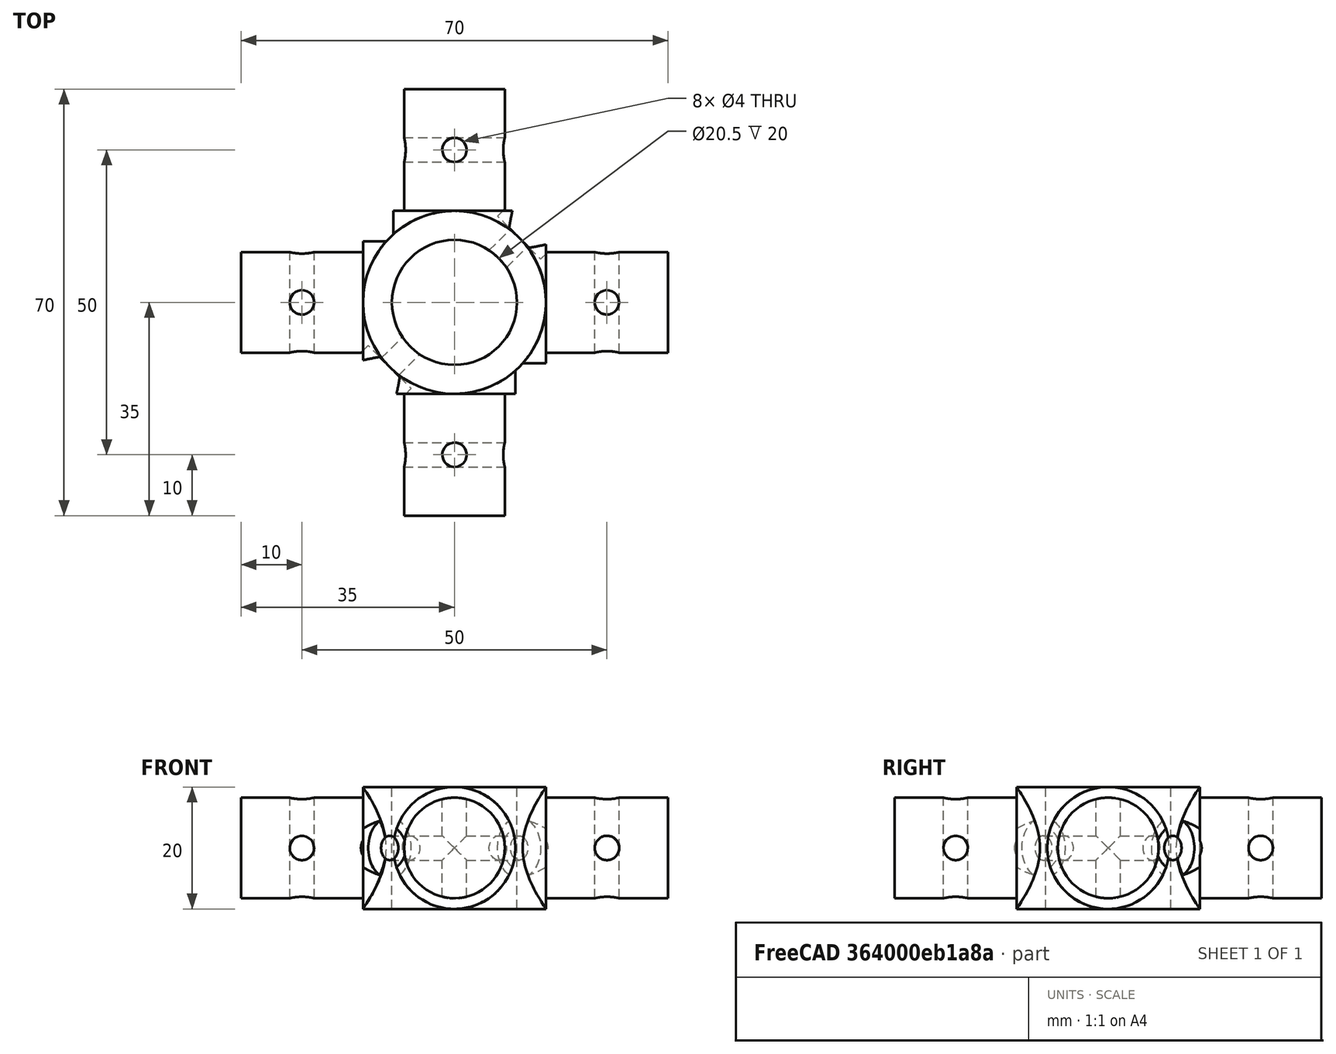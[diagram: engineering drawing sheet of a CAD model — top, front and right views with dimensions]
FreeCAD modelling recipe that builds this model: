
FCSTD DOCUMENT  (FreeCAD 0.18R16110 (Git))
Label: StandCross
License: All rights reserved
LicenseURL: http://en.wikipedia.org/wiki/All_rights_reserved
objects: Part::Cylinder×19, Part::MultiFuse×3, Part::Cut×1
note: 23 computed .brp shape members not serialized (recipe doc carries the construction recipe); baked Part::Feature solids carry a one-line shape summary decoded from their .brp

FEATURE [Part::Cylinder] Cylinder
  Angle = 360
  AttacherType = Attacher::AttachEngine3D
  Height = 20
  Radius = 15
FEATURE [Part::Cylinder] Cylinder001
  Angle = 360
  AttacherType = Attacher::AttachEngine3D
  Height = 20
  Placement = pos=(-15,-8.3e-15,10) rot=(-0.57735,-0.57735,0.57735;2.0944rad)
  Radius = 8.25
FEATURE [Part::Cylinder] Cylinder002
  Angle = 360
  AttacherType = Attacher::AttachEngine3D
  Height = 20
  Placement = pos=(0,15,10) rot=(-1,0,0;1.5708rad)
  Radius = 8.25
FEATURE [Part::Cylinder] Cylinder003
  Angle = 360
  AttacherType = Attacher::AttachEngine3D
  Height = 20
  Placement = pos=(15,5e-15,10) rot=(0.57735,-0.57735,0.57735;4.18879rad)
  Radius = 8.25
FEATURE [Part::Cylinder] Cylinder004
  Angle = 360
  AttacherType = Attacher::AttachEngine3D
  Height = 20
  Placement = pos=(9e-15,-15,10) rot=(0,0.707107,-0.707107;3.14159rad)
  Radius = 8.25
FEATURE [Part::Cylinder] Cylinder005
  Angle = 360
  AttacherType = Attacher::AttachEngine3D
  Height = 30
  Placement = pos=(-15,-3.1e-15,10) rot=(0.57735,-0.57735,0.57735;4.18879rad)
  Radius = 10
FEATURE [Part::Cylinder] Cylinder006
  Angle = 360
  AttacherType = Attacher::AttachEngine3D
  Height = 30
  Placement = pos=(9e-15,-15,10) rot=(-1,0,0;1.5708rad)
  Radius = 10
FEATURE [Part::MultiFuse] Fusion  label="Positive Fusion"
  Shapes = -> [Cylinder,Cylinder005,Cylinder002,Cylinder001,Cylinder003,Cylinder004,Cylinder006]
FEATURE [Part::Cylinder] Cylinder007
  Angle = 360
  AttacherType = Attacher::AttachEngine3D
  Height = 20
  Radius = 10.25
FEATURE [Part::Cylinder] Cylinder009
  Angle = 360
  AttacherType = Attacher::AttachEngine3D
  Height = 30
  Placement = pos=(-15,0,10) rot=(0,1,0;1.5708rad)
  Radius = 2
FEATURE [Part::Cylinder] Cylinder010
  Angle = 360
  AttacherType = Attacher::AttachEngine3D
  Height = 10
  Placement = pos=(15,0,10) rot=(0,1,0;1.5708rad)
  Radius = 5
FEATURE [Part::Cylinder] Cylinder011
  Angle = 360
  AttacherType = Attacher::AttachEngine3D
  Height = 10
  Placement = pos=(-15,0,10) rot=(0,1,0;4.71239rad)
  Radius = 5
FEATURE [Part::MultiFuse] Fusion002
  Placement = pos=(0,0,0) rot=(0,0,1;0.785398rad)
  Shapes = -> [Cylinder009,Cylinder010,Cylinder011]
FEATURE [Part::Cylinder] Cylinder012
  Angle = 360
  AttacherType = Attacher::AttachEngine3D
  Height = 20
  Placement = pos=(-10,-25,10) rot=(0,1,0;1.5708rad)
  Radius = 2
FEATURE [Part::Cylinder] Cylinder013
  Angle = 360
  AttacherType = Attacher::AttachEngine3D
  Height = 20
  Placement = pos=(3.6e-15,-25,2.7e-15) rot=(0,0,1;0rad)
  Radius = 2
FEATURE [Part::Cylinder] Cylinder014
  Angle = 360
  AttacherType = Attacher::AttachEngine3D
  Height = 20
  Placement = pos=(-25,0,3e-15) rot=(0,0,1;0rad)
  Radius = 2
FEATURE [Part::Cylinder] Cylinder015
  Angle = 360
  AttacherType = Attacher::AttachEngine3D
  Height = 20
  Placement = pos=(3.6e-15,25,3e-15) rot=(0,0,1;0rad)
  Radius = 2
FEATURE [Part::Cylinder] Cylinder016
  Angle = 360
  AttacherType = Attacher::AttachEngine3D
  Height = 20
  Placement = pos=(25,0,3e-15) rot=(0,0,1;0rad)
  Radius = 2
FEATURE [Part::Cylinder] Cylinder017
  Angle = 360
  AttacherType = Attacher::AttachEngine3D
  Height = 20
  Placement = pos=(-10,25,10) rot=(0,1,0;1.5708rad)
  Radius = 2
FEATURE [Part::Cylinder] Cylinder018
  Angle = 360
  AttacherType = Attacher::AttachEngine3D
  Height = 20
  Placement = pos=(-25,-10,10) rot=(0.57735,-0.57735,-0.57735;4.18879rad)
  Radius = 2
FEATURE [Part::Cylinder] Cylinder019
  Angle = 360
  AttacherType = Attacher::AttachEngine3D
  Height = 20
  Placement = pos=(25,-10,10) rot=(0.57735,-0.57735,-0.57735;4.18879rad)
  Radius = 2
FEATURE [Part::MultiFuse] Fusion001  label="Negative Fusion"
  Shapes = -> [Cylinder007,Fusion002,Cylinder012,Cylinder013,Cylinder014,Cylinder015,Cylinder016,Cylinder017,Cylinder018,Cylinder019]
FEATURE [Part::Cut] Cut
  Base = -> Fusion
  Tool = -> Fusion001
